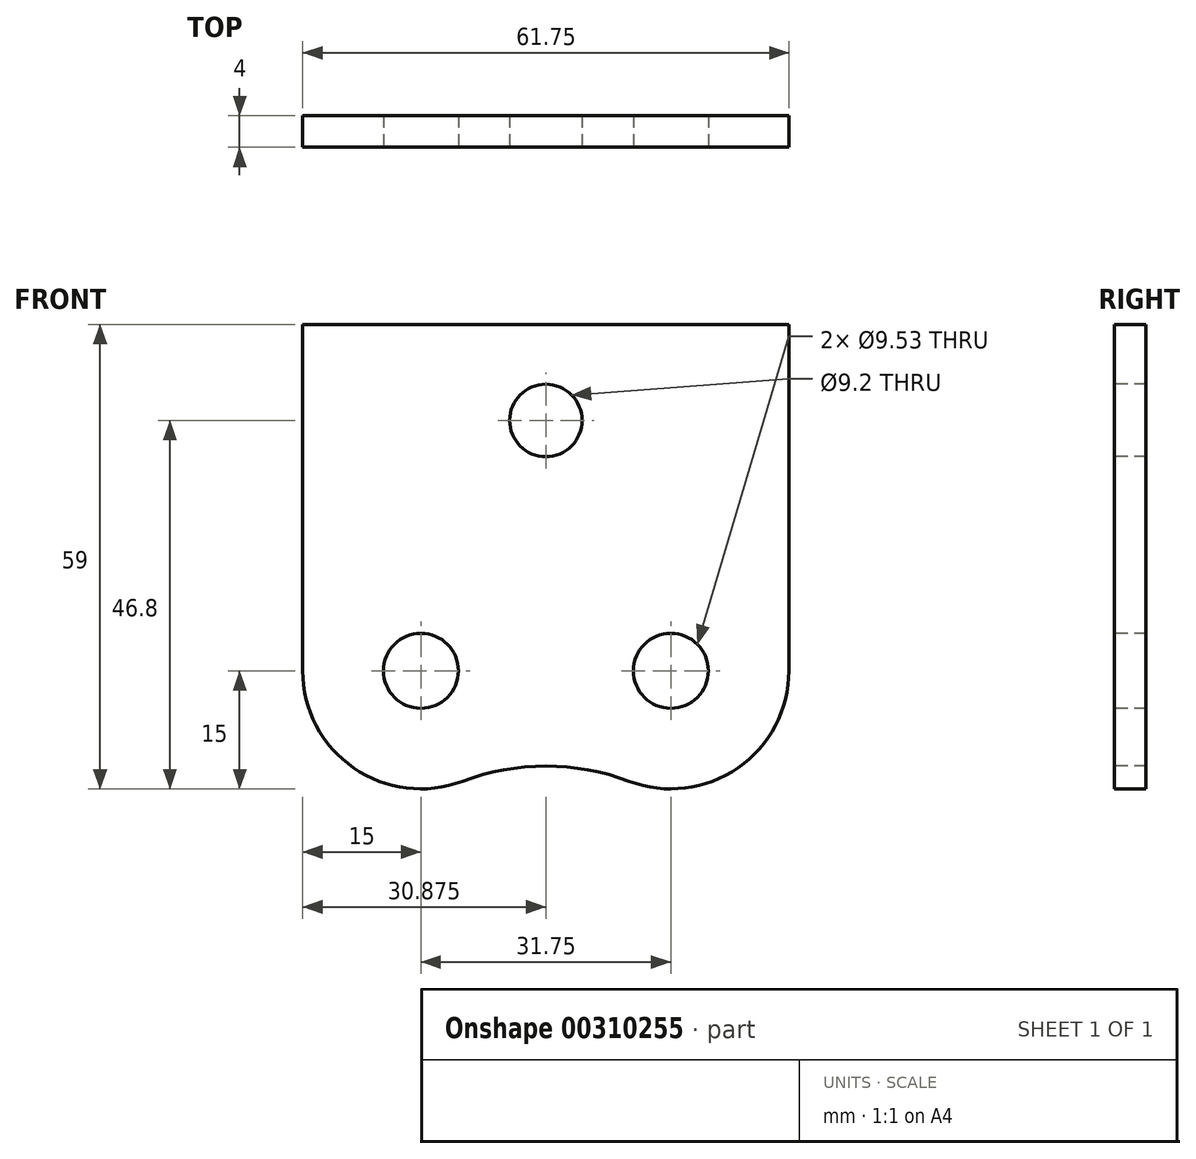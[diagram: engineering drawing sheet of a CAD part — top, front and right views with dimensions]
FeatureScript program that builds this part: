
annotation { "Feature Type Name" : "Feature", "Feature Type Description" : "" }
export const myFeature = defineFeature(function(context is Context, id is Id, definition is map)
    precondition{}
    {
        {
            var Q0;
            Q0=qCreatedBy(makeId("Front.planeOp"),FACE);
            var sketch = newSketch(context, id + "F0", { "sketchPlane" : qUnion([Q0])});
            skCircle(sketch, "E0", {"center": v(-31.75, 0) * mm, "radius": 4.77 * mm});
            skCircle(sketch, "E1", {"center": v(0, 0) * mm, "radius": 4.77 * mm});
            skArc(sketch, "E2", {"start": v(-46.75, 0) * mm, "mid": v(-40.28, -12.34) * mm, "end": v(-26.46, -14.04) * mm});
            skArc(sketch, "E3", {"start": v(-5.3, -14.04) * mm, "mid": v(8.53, -12.34) * mm, "end": v(15, 0) * mm});
            skArc(sketch, "E4", {"start": v(-5.3, -14.04) * mm, "mid": v(-15.88, -12.1) * mm, "end": v(-26.46, -14.04) * mm});
            skLineSegment(sketch, "E5.bottom", {"start": v(-36.52, 0) * mm, "end": v(-26.99, 0) * mm});
            skLineSegment(sketch, "E6.trimOffspring", {"start": v(-4.76, 0) * mm, "end": v(10.9, 0) * mm});
            skLineSegment(sketch, "E7.left", {"start": v(-46.75, 0) * mm, "end": v(-46.75, 31.8) * mm});
            skLineSegment(sketch, "E7.right", {"start": v(15, 0) * mm, "end": v(15, 31.8) * mm});
            skLineSegment(sketch, "E8.top", {"start": v(-46.75, 44) * mm, "end": v(15, 44) * mm});
            skLineSegment(sketch, "E8.left", {"start": v(-46.75, 0) * mm, "end": v(-46.75, 44) * mm});
            skLineSegment(sketch, "E8.right", {"start": v(15, 0) * mm, "end": v(15, 44) * mm});
            skCircle(sketch, "E9", {"center": v(-15.88, 31.8) * mm, "radius": 4.6 * mm});
            skSolve(sketch);
        }
        {
            var Q0;
            {var subQ1=sQuery(id+"F0.wireOp",EDGE,"E2");Q0=makeQuery(id+"F0.imprint","IMPRINT",FACE,{"disambiguationData":[TD([[makeQuery(id+"F0.imprint","IMPRINT",EDGE,{"derivedFrom":subQ1}),1.0]])]});}
            extrude(context, id + "F1", {"entities" : qUnion([Q0]), "oppositeDirection" : true, "depth" : 4 * mm});
        }
    });
